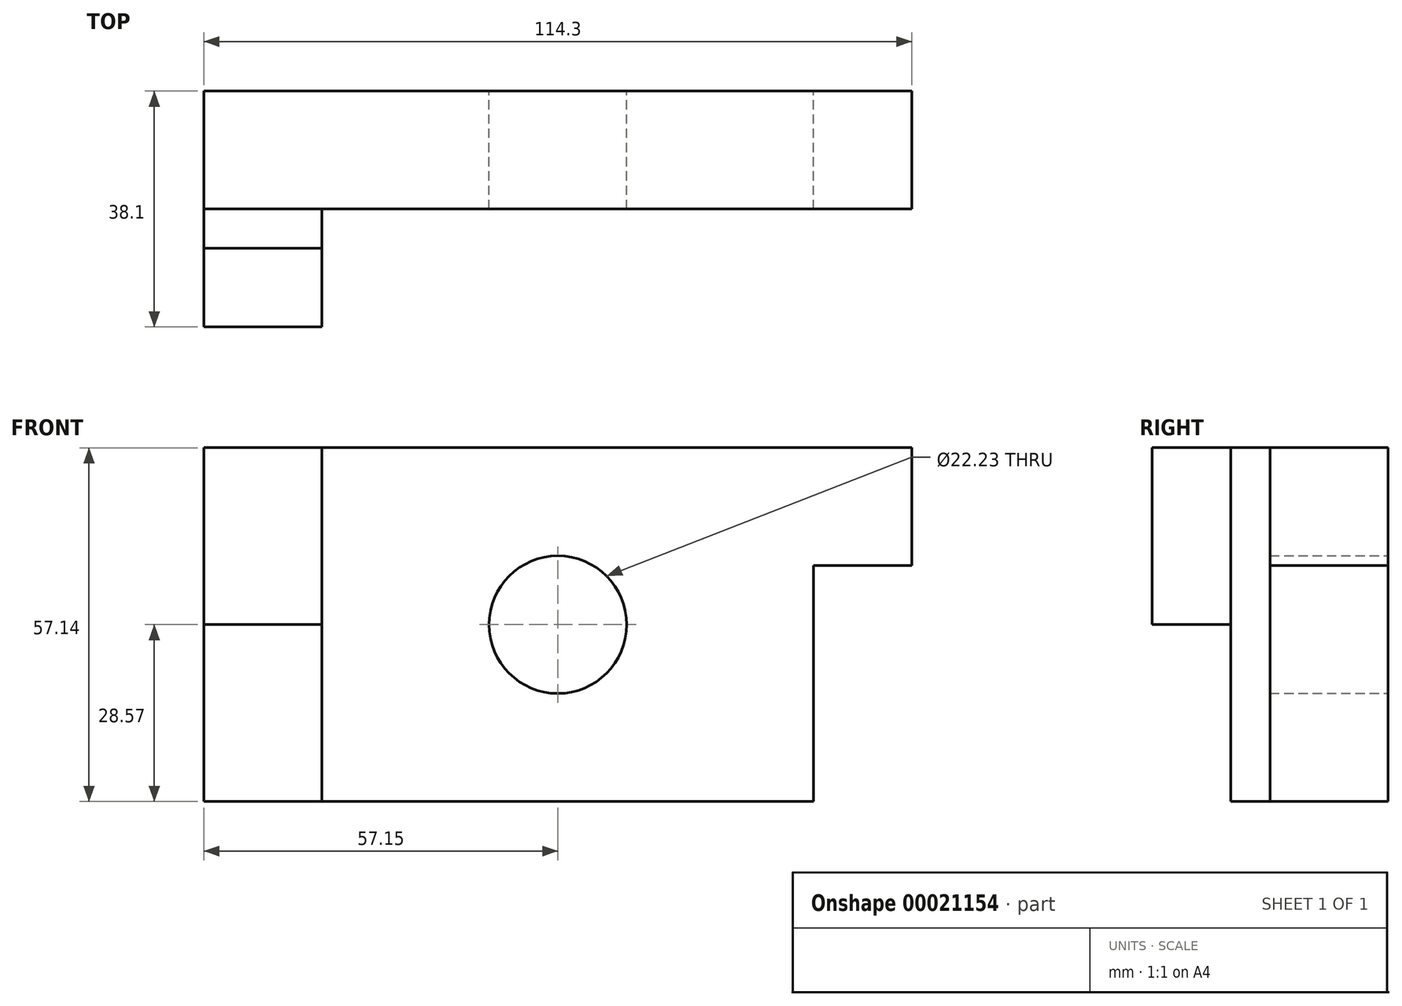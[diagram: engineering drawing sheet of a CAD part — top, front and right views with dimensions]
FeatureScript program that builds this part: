
annotation { "Feature Type Name" : "Feature", "Feature Type Description" : "" }
export const myFeature = defineFeature(function(context is Context, id is Id, definition is map)
    precondition{}
    {
        {
            var Q0;
            Q0=qCreatedBy(makeId("Front.planeOp"),FACE);
            var sketch = newSketch(context, id + "F0", { "sketchPlane" : qUnion([Q0])});
            skLineSegment(sketch, "E0.rect.bottom", {"start": v(-57.15, 28.58) * mm, "end": v(57.15, 28.58) * mm});
            skLineSegment(sketch, "E0.rect.top", {"start": v(-57.15, -28.58) * mm, "end": v(57.15, -28.58) * mm});
            skLineSegment(sketch, "E0.rect.left", {"start": v(-57.15, 28.58) * mm, "end": v(-57.15, -28.58) * mm});
            skLineSegment(sketch, "E0.rect.right", {"start": v(57.15, 28.58) * mm, "end": v(57.15, -28.58) * mm});
            skPoint(sketch, "E0.rect.middle", {"position": v(0, 0) * mm});
            skCircle(sketch, "E1", {"center": v(0, 0) * mm, "radius": 11.11 * mm});
            skLineSegment(sketch, "E2.bottom", {"start": v(57.15, -28.58) * mm, "end": v(41.27, -28.58) * mm});
            skLineSegment(sketch, "E2.top", {"start": v(57.15, 9.52) * mm, "end": v(41.27, 9.52) * mm});
            skLineSegment(sketch, "E2.left", {"start": v(57.15, -28.58) * mm, "end": v(57.15, 9.52) * mm});
            skLineSegment(sketch, "E2.right", {"start": v(41.27, -28.58) * mm, "end": v(41.27, 9.52) * mm});
            skSolve(sketch);
        }
        {
            var Q0;
            Q0=makeQuery(id+"F0.imprint","IMPRINT",FACE,{"disambiguationData":[TD([[makeQuery(id+"F0.imprint","IMPRINT",EDGE,{"derivedFrom":sQuery(id+"F0.wireOp",EDGE,"E0.rect.bottom")}),-1.0]])]});
            extrude(context, id + "F1", {"entities" : qUnion([Q0]), "depth" : 19.05 * mm});
        }
        {
            var Q0;
            Q0=makeQuery(id+"F1.opExtrude","CAP_FACE",FACE,{"disambiguationData":[OSD([sQuery(id+"F0.wireOp",EDGE,"E0.rect.bottom"),sQuery(id+"F0.wireOp",EDGE,"E0.rect.top"),sQuery(id+"F0.wireOp",EDGE,"E0.rect.left"),sQuery(id+"F0.wireOp",EDGE,"E0.rect.right"),sQuery(id+"F0.wireOp",EDGE,"E1"),sQuery(id+"F0.wireOp",EDGE,"E2.top"),sQuery(id+"F0.wireOp",EDGE,"E2.right")])],"isStart":false});
            var sketch = newSketch(context, id + "F2", { "sketchPlane" : qUnion([Q0])});
            skLineSegment(sketch, "E3.bottom", {"start": v(-57.15, 28.58) * mm, "end": v(-38.1, 28.58) * mm});
            skLineSegment(sketch, "E3.top", {"start": v(-57.15, -28.58) * mm, "end": v(-38.1, -28.58) * mm});
            skLineSegment(sketch, "E3.left", {"start": v(-57.15, 28.58) * mm, "end": v(-57.15, -28.58) * mm});
            skLineSegment(sketch, "E3.right", {"start": v(-38.1, 28.58) * mm, "end": v(-38.1, -28.58) * mm});
            skSolve(sketch);
        }
        {
            var Q0;
            Q0=makeQuery(id+"F2.imprint","IMPRINT",FACE,{"disambiguationData":[TD([[makeQuery(id+"F2.imprint","IMPRINT",EDGE,{"derivedFrom":sQuery(id+"F2.wireOp",EDGE,"E3.bottom")}),-1.0]])]});
            extrude(context, id + "F3", {"entities" : qUnion([Q0]), "depth" : 6.35 * mm});
        }
        {
            var Q0;
            Q0=makeQuery(id+"F3.opExtrude","CAP_FACE",FACE,{"disambiguationData":[OSD([sQuery(id+"F2.wireOp",EDGE,"E3.bottom"),sQuery(id+"F2.wireOp",EDGE,"E3.top"),sQuery(id+"F2.wireOp",EDGE,"E3.left"),sQuery(id+"F2.wireOp",EDGE,"E3.right")])],"isStart":false});
            var sketch = newSketch(context, id + "F4", { "sketchPlane" : qUnion([Q0])});
            skLineSegment(sketch, "E4.bottom", {"start": v(-57.15, 28.58) * mm, "end": v(-38.1, 28.58) * mm});
            skLineSegment(sketch, "E4.top", {"start": v(-57.15, 0) * mm, "end": v(-38.1, 0) * mm});
            skLineSegment(sketch, "E4.left", {"start": v(-57.15, 28.58) * mm, "end": v(-57.15, 0) * mm});
            skLineSegment(sketch, "E4.right", {"start": v(-38.1, 28.58) * mm, "end": v(-38.1, 0) * mm});
            skSolve(sketch);
        }
        {
            var Q0;
            Q0 = qSketchRegion(id + "F4", true);
            extrude(context, id + "F5", {"entities" : qUnion([Q0]), "depth" : 12.7 * mm});
        }
    });
